FCSTD DOCUMENT  (FreeCAD 1.0R39319 (Git))
Label: demo2
License: All rights reserved
LicenseURL: https://en.wikipedia.org/wiki/All_rights_reserved
objects: Sketcher::SketchObject×1, PartDesign::Body×1
note: 3 computed .brp shape members not serialized (recipe doc carries the construction recipe); baked Part::Feature solids carry a one-line shape summary decoded from their .brp

FEATURE [Sketcher::SketchObject] Sketch
  ArcFitTolerance = 1e-06
  AttachmentSupport = -> [XY_Plane]
  FullyConstrained = false
  MakeInternals = false
  MapMode = 5
  sketch-geometry (10):
    g0: ArcOfCircle CenterX=-45.0058 CenterY=-0.0330015 CenterZ=0 NormalX=0 NormalY=0 NormalZ=1 AngleXU=0 Radius=8.11887 StartAngle=1.7615 EndAngle=4.4056
    g1: Circle CenterX=-45 CenterY=0 CenterZ=0 NormalX=0 NormalY=0 NormalZ=1 AngleXU=0 Radius=7.14495
    g2: ArcOfCircle CenterX=44.7562 CenterY=-0.0107982 CenterZ=0 NormalX=0 NormalY=0 NormalZ=1 AngleXU=0 Radius=8.11887 StartAngle=4.98104 EndAngle=7.64502
    g3: Circle CenterX=45 CenterY=0 CenterZ=0 NormalX=0 NormalY=0 NormalZ=1 AngleXU=0 Radius=7.14495
    g4: ArcOfCircle CenterX=-3.08121 CenterY=-1.42051 CenterZ=0 NormalX=0 NormalY=0 NormalZ=1 AngleXU=0 Radius=19.4572 StartAngle=4.4056 EndAngle=4.98104
    g5: LineSegment StartX=-46.5455 StartY=7.94891 StartZ=0 EndX=-7.7179 EndY=17.4761 EndZ=0
    g6: LineSegment StartX=-47.4577 StartY=-7.7728 StartZ=0 EndX=-8.95716 EndY=-19.9692 EndZ=0
    g7: LineSegment StartX=2.10217 StartY=17.3335 StartZ=0 EndX=46.4404 EndY=7.93147 EndZ=0
    g8: LineSegment StartX=2.08329 StartY=-20.1797 StartZ=0 EndX=46.9112 EndY=-7.83845 EndZ=0
    g9: ArcOfCircle CenterX=-3.08121 CenterY=-1.42051 CenterZ=0 NormalX=0 NormalY=0 NormalZ=1 AngleXU=0 Radius=19.4572 StartAngle=1.30114 EndAngle=1.81141
  constraints (15):
    c: Equal(g0,g2)
    c: Equal(g1,g3)
    c: Symmetric(g1,g3,g-2)
    c: Coincident(g5,g9) = 1.5708
    c: Tangent(g6,g4) = -1.5708
    c: PointOnObject(g7,g9)
    c: Equal(g4,g9)
    c: PointOnObject(g9,g7)
    c: Coincident(g4,g9)
    c: Tangent(g2,g7) = 1.5708
    c: Tangent(g2,g8) = -1.5708
    c: Tangent(g4,g8) = -1.5708
    c: Tangent(g9,g5,g5) = 1.5708
    c: Tangent(g6,g0) = -1.5708
    c: Tangent(g5,g0)
FEATURE [PartDesign::Body] Body
  AllowCompound = false
  Group = -> [Sketch]
  Origin = -> Origin
